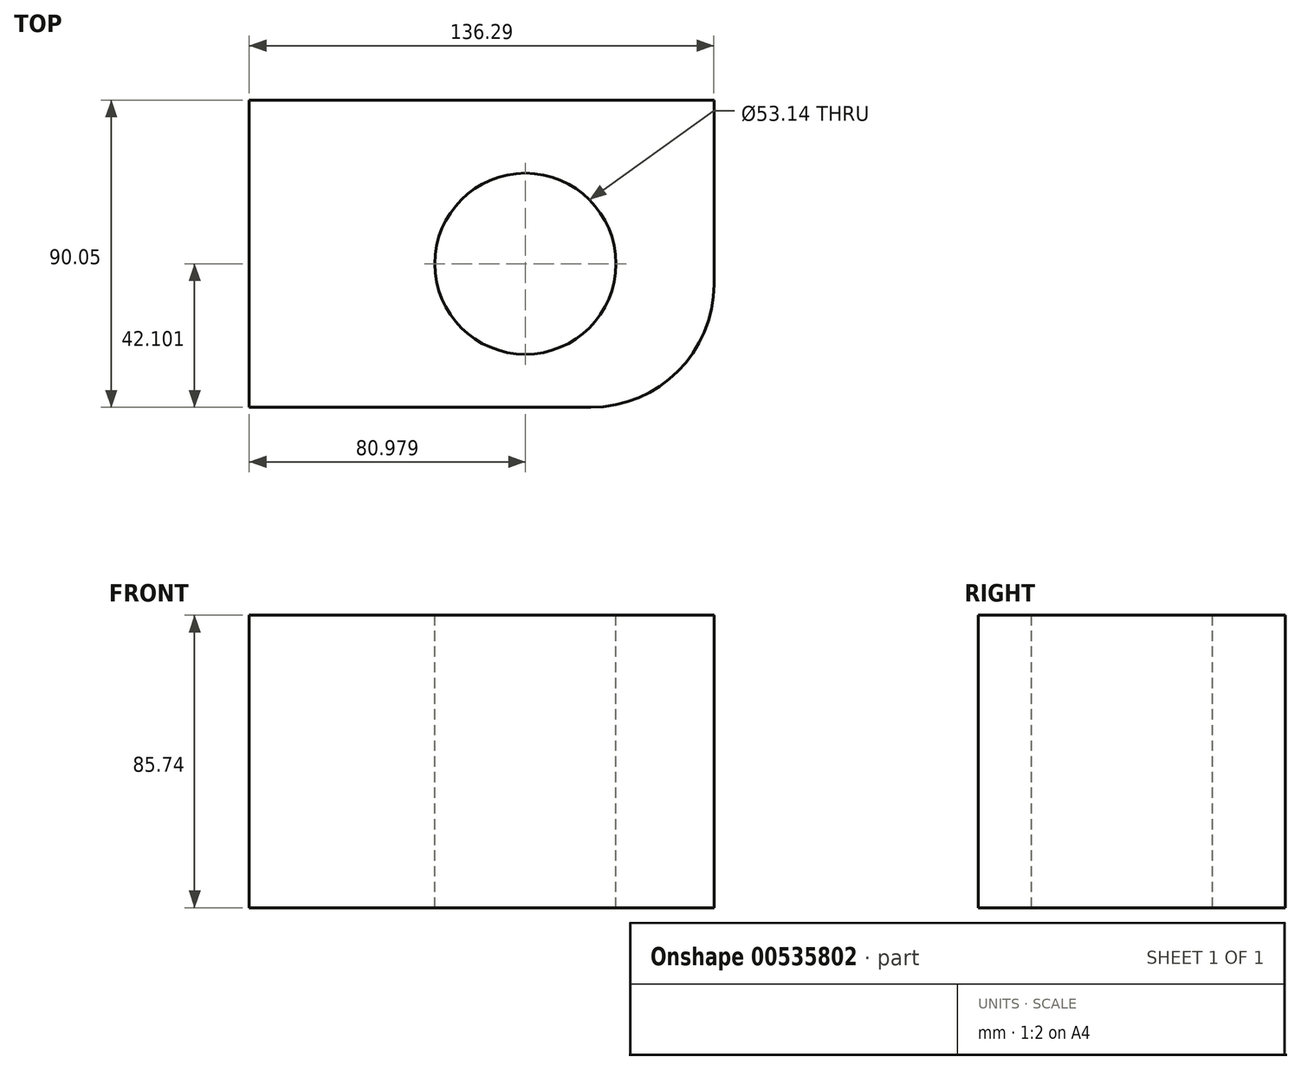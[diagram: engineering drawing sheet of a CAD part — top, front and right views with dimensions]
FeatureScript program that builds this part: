
annotation { "Feature Type Name" : "Feature", "Feature Type Description" : "" }
export const myFeature = defineFeature(function(context is Context, id is Id, definition is map)
    precondition{}
    {
        {
            var Q0;
            Q0=qCreatedBy(makeId("Front.planeOp"),FACE);
            var sketch = newSketch(context, id + "F0", { "sketchPlane" : qUnion([Q0])});
            skLineSegment(sketch, "E0.bottom", {"start": v(-53.48, 43.6) * mm, "end": v(82.81, 43.6) * mm});
            skLineSegment(sketch, "E0.top", {"start": v(-53.48, -42.14) * mm, "end": v(82.81, -42.14) * mm});
            skLineSegment(sketch, "E0.left", {"start": v(-53.48, 43.6) * mm, "end": v(-53.48, -42.14) * mm});
            skLineSegment(sketch, "E0.right", {"start": v(82.81, 43.6) * mm, "end": v(82.81, -42.14) * mm});
            skSolve(sketch);
        }
        {
            var Q0;
            Q0 = qSketchRegion(id + "F0", true);
            extrude(context, id + "F1", {"entities" : qUnion([Q0]), "depth" : 90.05 * mm, "offsetDistance" : 25.4 * mm});
        }
        {
            var Q0;
            Q0=makeQuery(id+"F1.opExtrude","SWEPT_FACE",FACE,{"disambiguationData":[OSD([sQuery(id+"F0.wireOp",EDGE,"E0.bottom")])]});
            var sketch = newSketch(context, id + "F2", { "sketchPlane" : qUnion([Q0])});
            skCircle(sketch, "E1", {"center": v(27.5, -47.95) * mm, "radius": 26.57 * mm});
            skSolve(sketch);
        }
        {
            var Q0;
            Q0=makeQuery(id+"F2.imprint","IMPRINT",FACE,{"disambiguationData":[TD([[makeQuery(id+"F2.imprint","IMPRINT",EDGE,{"derivedFrom":sQuery(id+"F2.wireOp",EDGE,"E1")}),1.0]])]});
            extrude(context, id + "F3", {"entities" : qUnion([Q0]), "operationType" : NewBodyOperationType.REMOVE, "oppositeDirection" : true, "depth" : 175.13 * mm, "offsetDistance" : 25.4 * mm});
        }
        {
            var Q0;
            Q0=makeQuery(id+"F1.opExtrude","CAP_EDGE",EDGE,{"disambiguationData":[OSD([sQuery(id+"F0.wireOp",EDGE,"E0.right")])],"isStart":false});
            fillet(context, id + "F4", {"entities" : qUnion([Q0]), "radius" : 36.1 * mm, "tangentPropagation" : true, "allowEdgeOverflow" : false});
        }
    });
